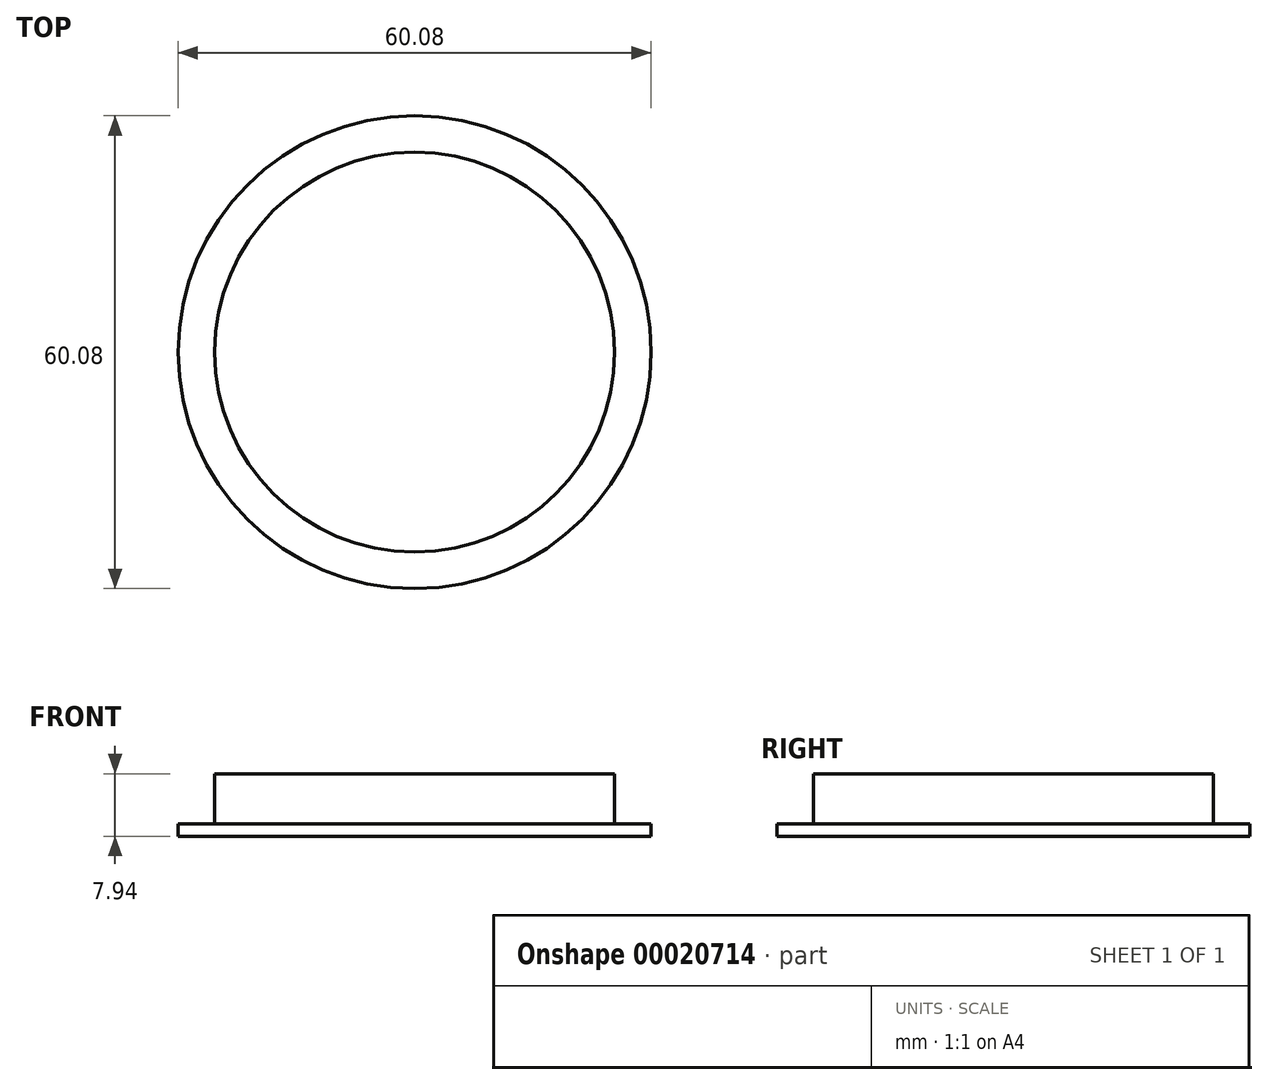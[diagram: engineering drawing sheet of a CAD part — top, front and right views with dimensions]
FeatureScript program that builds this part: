
annotation { "Feature Type Name" : "Feature", "Feature Type Description" : "" }
export const myFeature = defineFeature(function(context is Context, id is Id, definition is map)
    precondition{}
    {
        {
            var Q0;
            Q0=qCreatedBy(makeId("Top.planeOp"),FACE);
            var sketch = newSketch(context, id + "F0", { "sketchPlane" : qUnion([Q0])});
            skCircle(sketch, "E0", {"center": v(0, 0) * mm, "radius": 30.04 * mm});
            skSolve(sketch);
        }
        {
            var Q0;
            Q0 = qSketchRegion(id + "F0", true);
            extrude(context, id + "F1", {"entities" : qUnion([Q0]), "depth" : 1.59 * mm});
        }
        {
            var Q0;
            Q0=makeQuery(id+"F1.opExtrude","CAP_FACE",FACE,{"disambiguationData":[OSD([sQuery(id+"F0.wireOp",EDGE,"E0")])],"isStart":false});
            var sketch = newSketch(context, id + "F2", { "sketchPlane" : qUnion([Q0])});
            skCircle(sketch, "E1", {"center": v(0, 0) * mm, "radius": 25.4 * mm});
            skSolve(sketch);
        }
        {
            var Q0;
            Q0=makeQuery(id+"F2.imprint","IMPRINT",FACE,{"disambiguationData":[TD([[makeQuery(id+"F2.imprint","IMPRINT",EDGE,{"derivedFrom":sQuery(id+"F2.wireOp",EDGE,"E1")}),1.0]])]});
            extrude(context, id + "F3", {"entities" : qUnion([Q0]), "operationType" : NewBodyOperationType.ADD, "depth" : 6.35 * mm});
        }
    });
